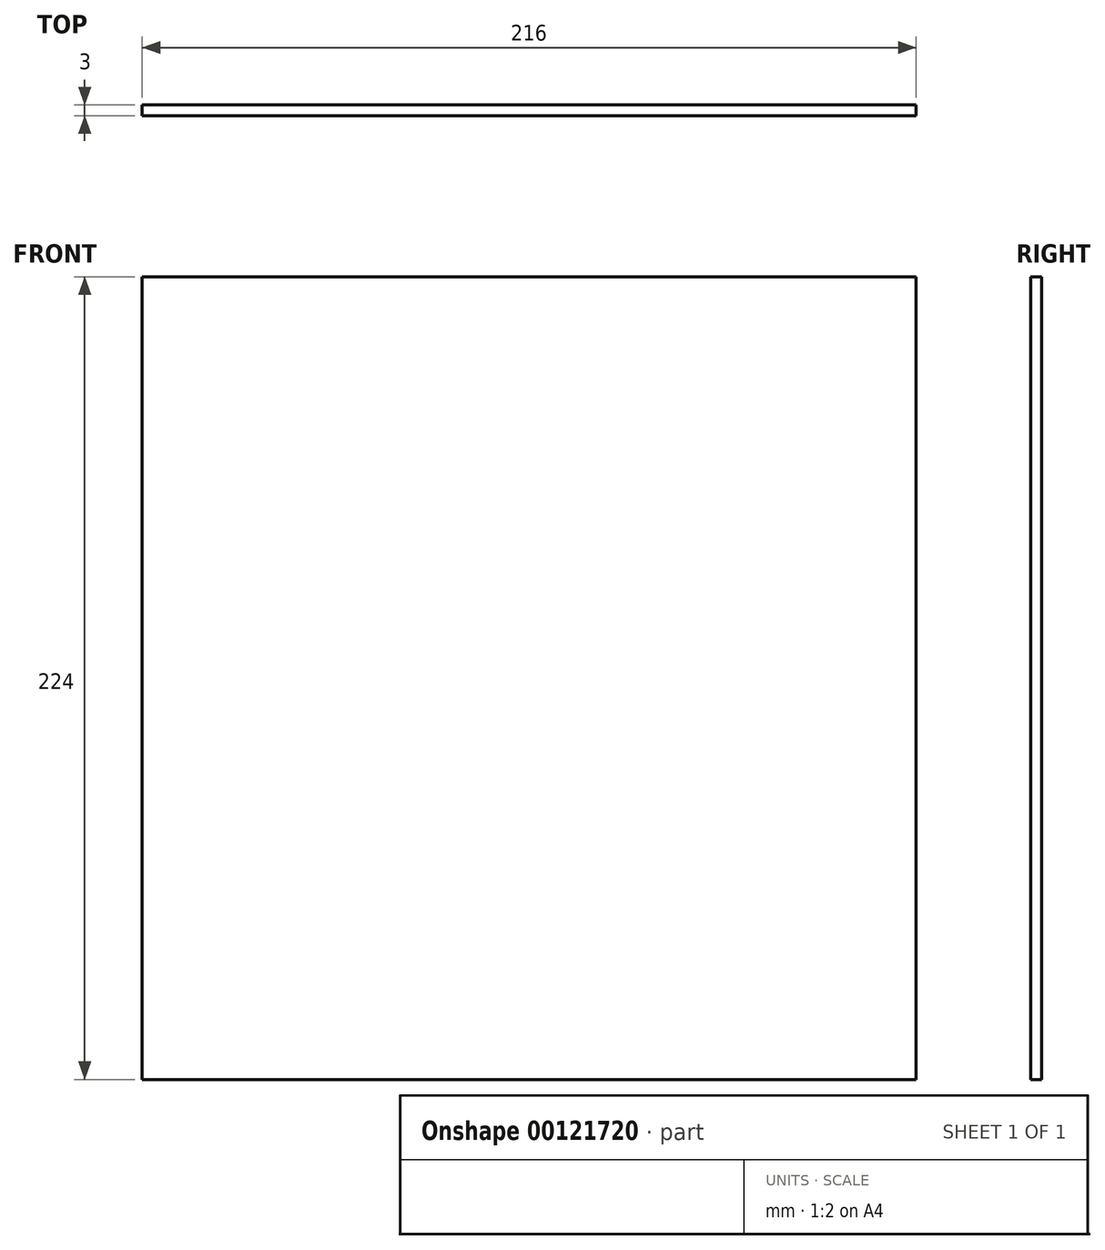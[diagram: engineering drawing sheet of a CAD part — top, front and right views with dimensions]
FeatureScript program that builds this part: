
annotation { "Feature Type Name" : "Feature", "Feature Type Description" : "" }
export const myFeature = defineFeature(function(context is Context, id is Id, definition is map)
    precondition{}
    {
        {
            var Q0;
            Q0=qCreatedBy(makeId("Front.planeOp"),FACE);
            var sketch = newSketch(context, id + "F0", { "sketchPlane" : qUnion([Q0])});
            skLineSegment(sketch, "E0.bottom", {"start": v(0, 0) * mm, "end": v(216, 0) * mm});
            skLineSegment(sketch, "E0.top", {"start": v(0, 224) * mm, "end": v(216, 224) * mm});
            skLineSegment(sketch, "E0.left", {"start": v(0, 0) * mm, "end": v(0, 224) * mm});
            skLineSegment(sketch, "E0.right", {"start": v(216, 0) * mm, "end": v(216, 224) * mm});
            skSolve(sketch);
        }
        {
            var Q0;
            Q0 = qSketchRegion(id + "F0", true);
            var Q1;
            Q1=makeQuery(id+"F0.imprint","IMPRINT",FACE,{"disambiguationData":[TD([[makeQuery(id+"F0.imprint","IMPRINT",EDGE,{"derivedFrom":sQuery(id+"F0.wireOp",EDGE,"E0.bottom")}),1.0]])]});
            extrude(context, id + "F1", {"entities" : qUnion([Q0, Q1]), "depth" : 3 * mm});
        }
    });
